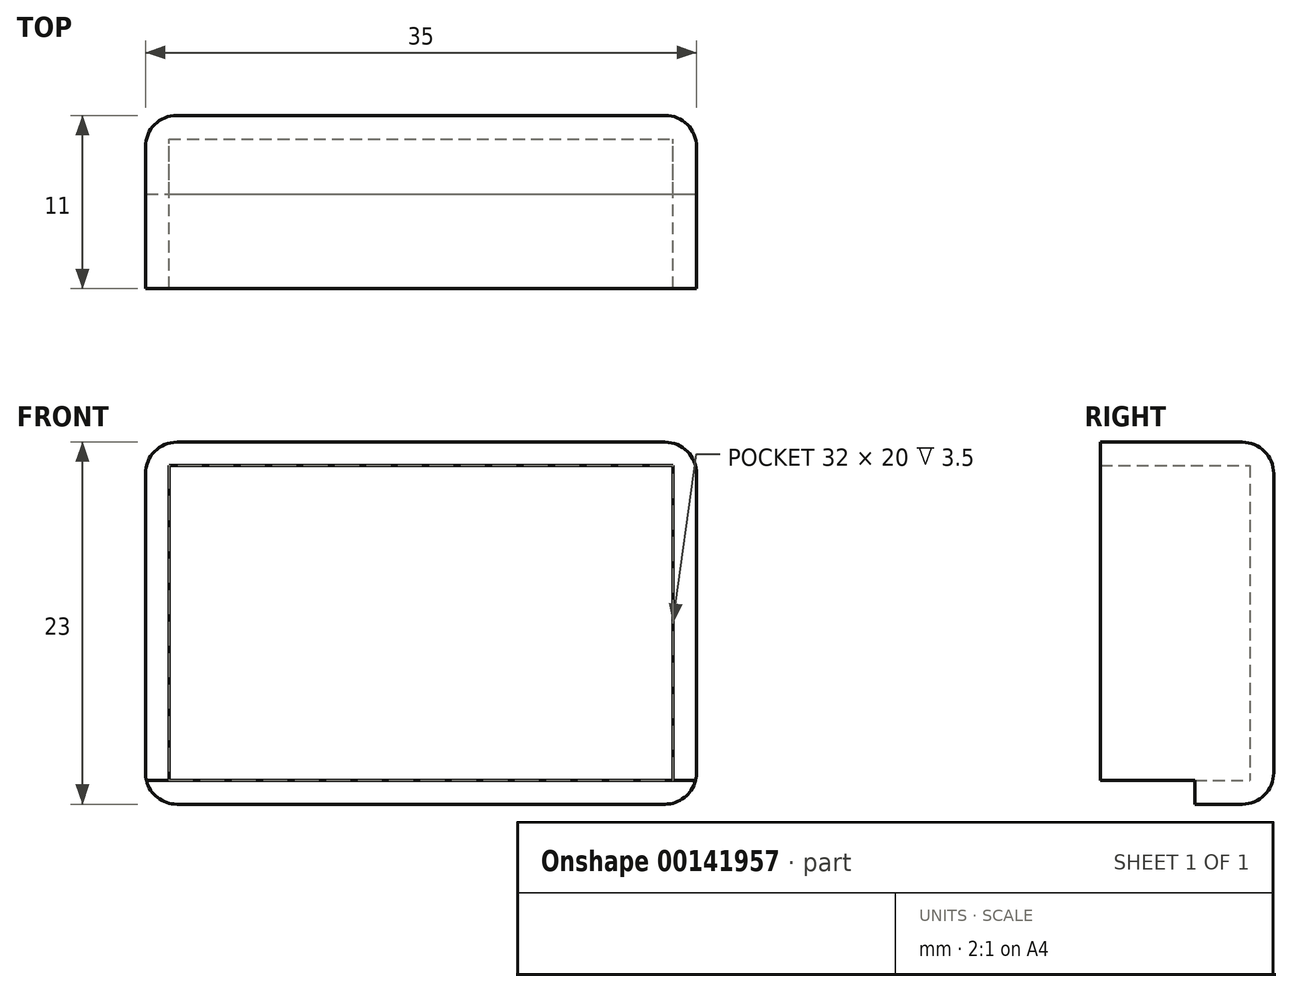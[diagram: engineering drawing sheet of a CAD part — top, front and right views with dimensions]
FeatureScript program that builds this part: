
annotation { "Feature Type Name" : "Feature", "Feature Type Description" : "" }
export const myFeature = defineFeature(function(context is Context, id is Id, definition is map)
    precondition{}
    {
        {
            var Q0;
            Q0=qCreatedBy(makeId("Front.planeOp"),FACE);
            var sketch = newSketch(context, id + "F0", { "sketchPlane" : qUnion([Q0])});
            skLineSegment(sketch, "E0.bottom", {"start": v(-15.54, 14.93) * mm, "end": v(16.46, 14.93) * mm});
            skLineSegment(sketch, "E0.top", {"start": v(-15.54, -5.07) * mm, "end": v(16.46, -5.07) * mm});
            skLineSegment(sketch, "E0.left", {"start": v(-15.54, 14.93) * mm, "end": v(-15.54, -5.07) * mm});
            skLineSegment(sketch, "E0.right", {"start": v(16.46, 14.93) * mm, "end": v(16.46, -5.07) * mm});
            skLineSegment(sketch, "E1.bottom", {"start": v(-17.04, 16.43) * mm, "end": v(17.96, 16.43) * mm});
            skLineSegment(sketch, "E1.top", {"start": v(-17.04, -6.57) * mm, "end": v(17.96, -6.57) * mm});
            skLineSegment(sketch, "E1.left", {"start": v(-17.04, 16.43) * mm, "end": v(-17.04, -6.57) * mm});
            skLineSegment(sketch, "E1.right", {"start": v(17.96, 16.43) * mm, "end": v(17.96, -6.57) * mm});
            skLineSegment(sketch, "E2", {"start": v(-15.54, -5.07) * mm, "end": v(-17.04, -5.07) * mm});
            skLineSegment(sketch, "E3", {"start": v(16.46, -5.07) * mm, "end": v(17.96, -5.07) * mm});
            skSolve(sketch);
        }
        {
            var Q0;
            Q0=makeQuery(id+"F0.imprint","IMPRINT",FACE,{"disambiguationData":[TD([[makeQuery(id+"F0.imprint","IMPRINT",EDGE,{"derivedFrom":sQuery(id+"F0.wireOp",EDGE,"E0.bottom")}),-1.0]])]});
            extrude(context, id + "F1", {"entities" : qUnion([Q0]), "depth" : 1.5 * mm});
        }
        {
            var Q0;
            Q0=makeQuery(id+"F0.imprint","IMPRINT",FACE,{"disambiguationData":[TD([[makeQuery(id+"F0.imprint","IMPRINT",EDGE,{"derivedFrom":sQuery(id+"F0.wireOp",EDGE,"E0.bottom")}),1.0]])]});
            extrude(context, id + "F2", {"entities" : qUnion([Q0]), "operationType" : NewBodyOperationType.ADD, "depth" : 11 * mm});
        }
        {
            var Q0;
            Q0=makeQuery(id+"F0.imprint","IMPRINT",FACE,{"disambiguationData":[TD([[makeQuery(id+"F0.imprint","IMPRINT",EDGE,{"derivedFrom":sQuery(id+"F0.wireOp",EDGE,"E0.top")}),-1.0]])]});
            extrude(context, id + "F3", {"entities" : qUnion([Q0]), "operationType" : NewBodyOperationType.ADD, "depth" : 5 * mm});
        }
        {
            var Q0;
            {var subQ0=sQuery(id+"F0.wireOp",EDGE,"E1.right");Q0=makeQuery(id+"F3.boolean.opBoolean","MERGE",EDGE,{"derivedFrom":[makeQuery(id+"F2.opExtrude","CAP_EDGE",EDGE,{"disambiguationData":[OSD([subQ0])],"isStart":true}),makeQuery(id+"F3.opExtrude","CAP_EDGE",EDGE,{"disambiguationData":[OSD([subQ0])],"isStart":true})]});}
            var Q1;
            Q1=makeQuery(id+"F2.opExtrude","CAP_EDGE",EDGE,{"disambiguationData":[OSD([sQuery(id+"F0.wireOp",EDGE,"E1.bottom")])],"isStart":true});
            var Q2;
            {var subQ0=sQuery(id+"F0.wireOp",EDGE,"E1.left");Q2=makeQuery(id+"F3.boolean.opBoolean","MERGE",EDGE,{"derivedFrom":[makeQuery(id+"F2.opExtrude","CAP_EDGE",EDGE,{"disambiguationData":[OSD([subQ0])],"isStart":true}),makeQuery(id+"F3.opExtrude","CAP_EDGE",EDGE,{"disambiguationData":[OSD([subQ0])],"isStart":true})]});}
            var Q3;
            Q3=makeQuery(id+"F3.opExtrude","CAP_EDGE",EDGE,{"disambiguationData":[OSD([sQuery(id+"F0.wireOp",EDGE,"E1.top")])],"isStart":true});
            var Q4;
            Q4=makeQuery(id+"F2.opExtrude","SWEPT_EDGE",EDGE,{"disambiguationData":[OSD([sQuery(id+"F0.wireOp",EDGE,"E1.bottom"),sQuery(id+"F0.wireOp",EDGE,"E1.right")])]});
            var Q5;
            Q5=makeQuery(id+"F2.opExtrude","SWEPT_EDGE",EDGE,{"disambiguationData":[OSD([sQuery(id+"F0.wireOp",EDGE,"E1.bottom"),sQuery(id+"F0.wireOp",EDGE,"E1.left")])]});
            fillet(context, id + "F4", {"entities" : qUnion([Q0, Q1, Q2, Q3, Q4, Q5]), "radius" : 2 * mm, "tangentPropagation" : true, "allowEdgeOverflow" : false});
        }
        {
            var Q0;
            Q0=makeQuery(id+"F3.opExtrude","SWEPT_EDGE",EDGE,{"disambiguationData":[OSD([sQuery(id+"F0.wireOp",EDGE,"E1.top"),sQuery(id+"F0.wireOp",EDGE,"E1.left")])]});
            var Q1;
            Q1=makeQuery(id+"F3.opExtrude","SWEPT_EDGE",EDGE,{"disambiguationData":[OSD([sQuery(id+"F0.wireOp",EDGE,"E1.top"),sQuery(id+"F0.wireOp",EDGE,"E1.right")])]});
            fillet(context, id + "F5", {"entities" : qUnion([Q0, Q1]), "radius" : 2 * mm, "tangentPropagation" : true, "allowEdgeOverflow" : false});
        }
    });
